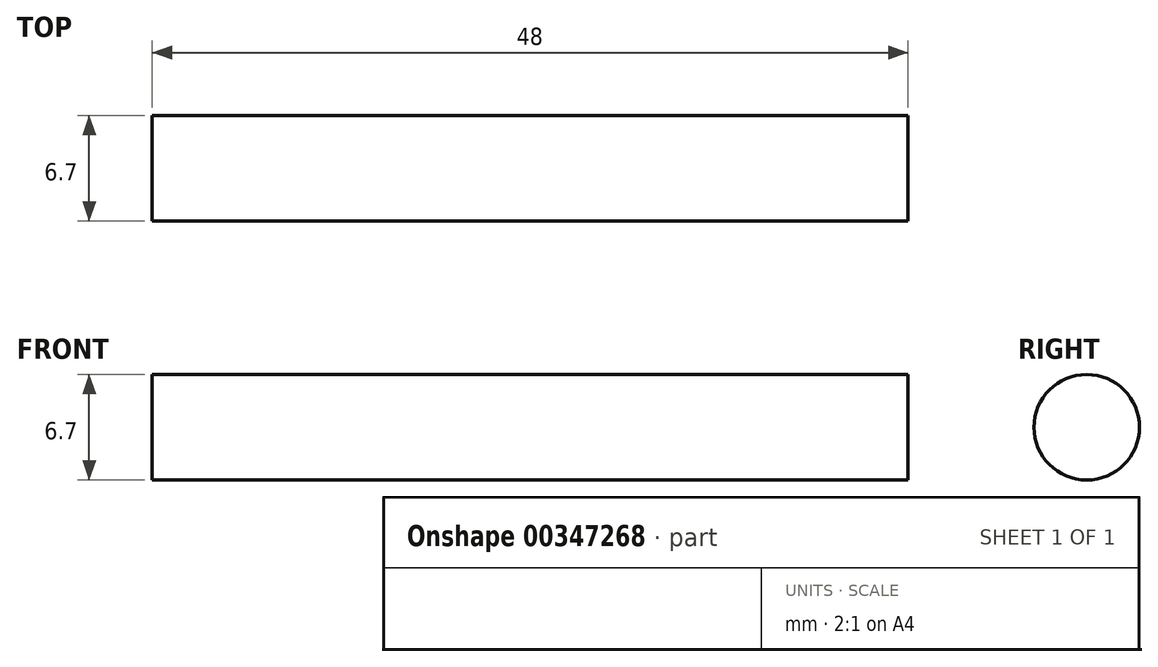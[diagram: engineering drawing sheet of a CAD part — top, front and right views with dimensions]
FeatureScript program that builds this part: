
annotation { "Feature Type Name" : "Feature", "Feature Type Description" : "" }
export const myFeature = defineFeature(function(context is Context, id is Id, definition is map)
    precondition{}
    {
        {
            var Q0;
            Q0=qCreatedBy(makeId("Right.planeOp"),FACE);
            var sketch = newSketch(context, id + "F0", { "sketchPlane" : qUnion([Q0])});
            skCircle(sketch, "E0", {"center": v(0, 0) * mm, "radius": 3.35 * mm});
            skSolve(sketch);
        }
        {
            var Q0;
            Q0 = qSketchRegion(id + "F0", true);
            extrude(context, id + "F1", {"entities" : qUnion([Q0]), "depth" : 48 * mm, "symmetric" : true});
        }
    });
